# Revit family: NBS_Allermuir_DmstcChrs_Mote_MTE-MEDTB12
name_source: partatom
category: Furniture
revit_build: Autodesk Revit 2016 (Build: 20161004_0715(x64)
units: mm (PartAtom-declared; Revit-internal decimal feet)

## family parameters
Always vertical = Yes
Cut with Voids When Loaded = No
Room Calculation Point = No
Shared = No
Work Plane-Based = No

## types (1)
- MTE-MEDTB012
    AssetType = Moveable
    BIMObjectName = NBS_Allermuir_DomesticChairs_Mote_MTE-MEDTB12
    Category = Pr_40_50_12_22:Dining chairs
    ColumnMaterial = NBS_Concept
    Description = Four/six seat table
    DurationUnit = year
    ExpectedLife = 5
    Features = 25 mm MFMDF top with a clear edge profile, available in all standard MFMDF, fully upholstered table support in fabric matching bridging screen, table support base plate finished in black powder coat, plastic glides, table support base plate available in flint grey, mineral sand, mellow yellow or orange crush powder coat, table edge profile can be stained
    FootHeight = 11 mm  [stored 0.0360892 ft]
    FrameMountingMaterial = NBS_Concept
    FrameShroudMaterial = NBS_Concept
    HighestSeatingHeight = 0 mm  [stored 0 ft]
    IfcExportAs = IfcFurnitureType
    IfcExportType = SOFA
    IsBuiltIn = No
    LowestSeatingHeight = 0 mm  [stored 0 ft]
    ManufacturerName = Allermuir
    ManufacturerURL = http://www.thesenatorgroup.com
    ModelNumber = MTE-MEDTB12
    ModelReference = Mote accessories
    NBSCertification = www.nationalbimlibrary.com/cert/b2lrmyzz
    NBSDescription = Domestic chairs
    NBSReference = 45-35-20/365
    Name = DomesticChairs_Mote_MTE-MEDTB12_Allermuir
    NominalDepth = 800 mm  [stored 2.62467 ft]
    NominalHeight = 740 mm  [stored 2.42782 ft]
    NominalLength = 1348 mm  [stored 4.42257 ft]
    NominalWidth = 800 mm  [stored 2.62467 ft]
    NumberOfChairs = 0
    PostHeight = 550 mm
    ProductInformation = http://www.thesenatorgroup.com
    SeatingHeight = 0 mm  [stored 0 ft]
    Size = 850 x 1350 x 735 mm
    Status = UNSET
    TableTopLength = 1348 mm  [stored 4.42257 ft]
    TableTopSupportRailMaterial = NBS_Concept
    TableTopWidth = 800 mm  [stored 2.62467 ft]
    Uniclass2015Code = Pr_40_50_12_22
    Uniclass2015Title = Dining chairs
    Uniclass2015Version = Products v1.9
    Version = 1
    WarrantyDescription = Allermuir warrant that its manufactured products are free from manufacturing defects in materials or workmanship for a period of five years
    WarrantyDurationParts = 5
    WarrantyDurationUnit = year
    WorksurfaceArea = 1.08 m²
    WorktopHeight = 740 mm  [stored 2.42782 ft]
    WorktopMFMDF = Yes
    WorktopMaterial = NBS_Concept
    WorktopMaterialTapedEdge = NBS_Concept
    WorktopThickness = 25 mm  [stored 0.082021 ft]
    WorktopType = NBS_Allermuir_DmstcChrs_Mote_MTE-MEDTB12MFMDF : MTE-MEDTB12MFMDF

note: [stored X ft] marks values corroborated as IEEE doubles in the binary element streams (Revit-internal decimal feet)

## geometry (parser evidence)
native form markers: Sweep x6
no freeform markers — native parametric forms only
